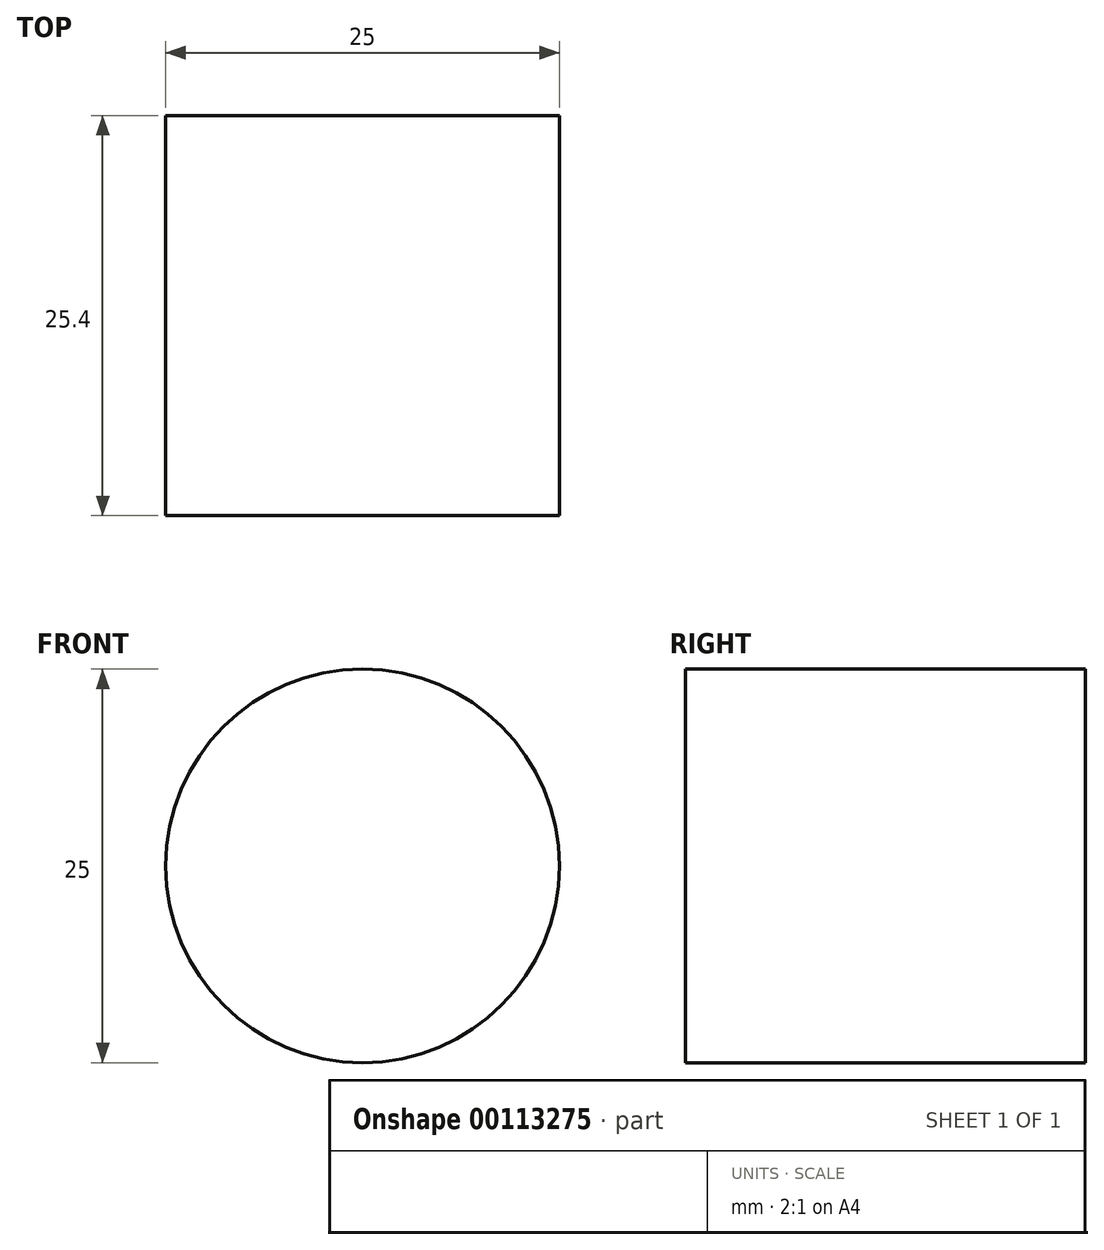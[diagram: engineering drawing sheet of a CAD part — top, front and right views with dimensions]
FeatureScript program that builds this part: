
annotation { "Feature Type Name" : "Feature", "Feature Type Description" : "" }
export const myFeature = defineFeature(function(context is Context, id is Id, definition is map)
    precondition{}
    {
        {
            var Q0;
            Q0=qCreatedBy(makeId("Front.planeOp"),FACE);
            var sketch = newSketch(context, id + "F0", { "sketchPlane" : qUnion([Q0])});
            skCircle(sketch, "E0", {"center": v(0, 0) * mm, "radius": 12.5 * mm});
            skSolve(sketch);
        }
        {
            var Q0;
            Q0 = qSketchRegion(id + "F0", true);
            extrude(context, id + "F1", {"entities" : qUnion([Q0]), "endBound" : BoundingType.SYMMETRIC, "depth" : 25.4 * mm});
        }
    });
